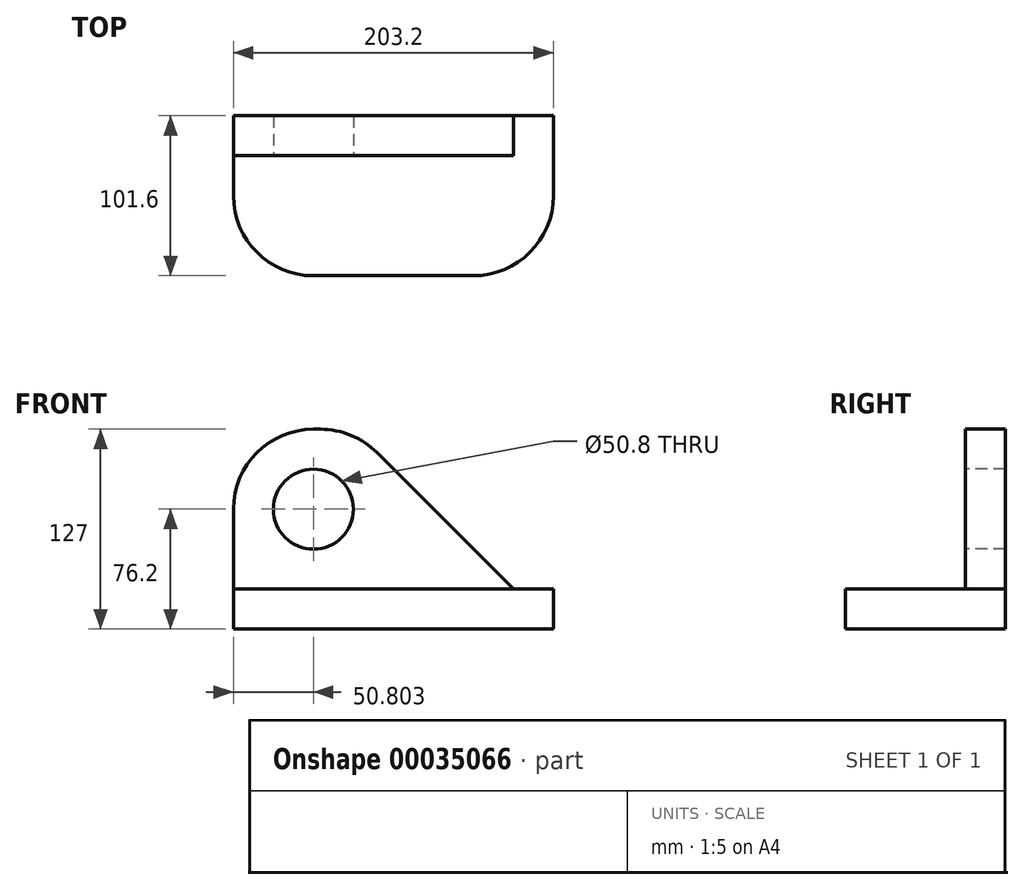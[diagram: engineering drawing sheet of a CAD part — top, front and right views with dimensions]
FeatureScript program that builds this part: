
annotation { "Feature Type Name" : "Feature", "Feature Type Description" : "" }
export const myFeature = defineFeature(function(context is Context, id is Id, definition is map)
    precondition{}
    {
        {
            var Q0;
            Q0=qCreatedBy(makeId("Top.planeOp"),FACE);
            var sketch = newSketch(context, id + "F0", { "sketchPlane" : qUnion([Q0])});
            skLineSegment(sketch, "E0.bottom", {"start": v(-49.18, 40.48) * mm, "end": v(154.02, 40.48) * mm});
            skLineSegment(sketch, "E0.top", {"start": v(-49.18, -61.12) * mm, "end": v(154.02, -61.12) * mm});
            skLineSegment(sketch, "E0.left", {"start": v(-49.18, 40.48) * mm, "end": v(-49.18, -61.12) * mm});
            skLineSegment(sketch, "E0.right", {"start": v(154.02, 40.48) * mm, "end": v(154.02, -61.12) * mm});
            skSolve(sketch);
        }
        {
            var Q0;
            Q0 = qSketchRegion(id + "F0", true);
            var Q1;
            Q1=makeQuery(id+"F0.imprint","IMPRINT",FACE,{"disambiguationData":[TD([[makeQuery(id+"F0.imprint","IMPRINT",EDGE,{"derivedFrom":sQuery(id+"F0.wireOp",EDGE,"E0.bottom")}),-1.0]])]});
            extrude(context, id + "F1", {"entities" : qUnion([Q0, Q1]), "depth" : 25.4 * mm});
        }
        {
            var Q0;
            Q0=makeQuery(id+"F1.opExtrude","SWEPT_EDGE",EDGE,{"disambiguationData":[OSD([sQuery(id+"F0.wireOp",EDGE,"E0.top"),sQuery(id+"F0.wireOp",EDGE,"E0.left")])]});
            var Q1;
            Q1=makeQuery(id+"F1.opExtrude","SWEPT_EDGE",EDGE,{"disambiguationData":[OSD([sQuery(id+"F0.wireOp",EDGE,"E0.top"),sQuery(id+"F0.wireOp",EDGE,"E0.right")])]});
            fillet(context, id + "F2", {"entities" : qUnion([Q0, Q1]), "radius" : 50.8 * mm, "tangentPropagation" : true, "allowEdgeOverflow" : false});
        }
        {
            var Q0;
            Q0=makeQuery(id+"F1.opExtrude","CAP_FACE",FACE,{"disambiguationData":[OSD([sQuery(id+"F0.wireOp",EDGE,"E0.bottom"),sQuery(id+"F0.wireOp",EDGE,"E0.top"),sQuery(id+"F0.wireOp",EDGE,"E0.left"),sQuery(id+"F0.wireOp",EDGE,"E0.right")])],"isStart":false});
            var sketch = newSketch(context, id + "F3", { "sketchPlane" : qUnion([Q0])});
            skLineSegment(sketch, "E1.bottom", {"start": v(-49.18, 40.48) * mm, "end": v(128.62, 40.48) * mm});
            skLineSegment(sketch, "E1.top", {"start": v(-49.18, 15.08) * mm, "end": v(128.62, 15.08) * mm});
            skLineSegment(sketch, "E1.left", {"start": v(-49.18, 40.48) * mm, "end": v(-49.18, 15.08) * mm});
            skLineSegment(sketch, "E1.right", {"start": v(128.62, 40.48) * mm, "end": v(128.62, 15.08) * mm});
            skSolve(sketch);
        }
        {
            var Q0;
            Q0=makeQuery(id+"F3.imprint","IMPRINT",FACE,{"disambiguationData":[TD([[makeQuery(id+"F3.imprint","IMPRINT",EDGE,{"derivedFrom":sQuery(id+"F3.wireOp",EDGE,"E1.bottom")}),-1.0]])]});
            extrude(context, id + "F4", {"entities" : qUnion([Q0]), "operationType" : NewBodyOperationType.ADD, "depth" : 25.4 * mm});
        }
        {
            var Q0;
            Q0 = qSketchRegion(id + "F3", true);
            extrude(context, id + "F5", {"entities" : qUnion([Q0]), "operationType" : NewBodyOperationType.ADD, "depth" : 101.6 * mm});
        }
        {
            var Q0;
            Q0=makeQuery(id+"F5.opExtrude","CAP_EDGE",EDGE,{"disambiguationData":[OSD([sQuery(id+"F3.wireOp",EDGE,"E1.right")])],"isStart":false});
            chamfer(context, id + "F6", {"entities" : qUnion([Q0]), "chamferType" : ChamferType.TWO_OFFSETS, "width1" : 101.6 * mm, "oppositeDirection" : false, "width2" : 101.6 * mm, "tangentPropagation" : true});
        }
        {
            var Q0;
            Q0=makeQuery(id+"F5.opExtrude","CAP_EDGE",EDGE,{"disambiguationData":[OSD([sQuery(id+"F3.wireOp",EDGE,"E1.left")])],"isStart":false});
            var Q1;
            {var subQ0=sQuery(id+"F3.wireOp",EDGE,"E1.right");Q1=makeQuery(id+"F6.opChamfer","BLEND_EDGE",EDGE,{"blendedFrom":[makeQuery(id+"F5.opExtrude","CAP_EDGE",EDGE,{"disambiguationData":[OSD([subQ0])],"isStart":false}),makeQuery(id+"F5.opExtrude","CAP_FACE",FACE,{"disambiguationData":[OSD([sQuery(id+"F3.wireOp",EDGE,"E1.bottom"),sQuery(id+"F3.wireOp",EDGE,"E1.top"),sQuery(id+"F3.wireOp",EDGE,"E1.left"),subQ0])],"isStart":false})],"blendedInto":[makeQuery(id+"F5.opExtrude","CAP_FACE",FACE,{"disambiguationData":[OSD([sQuery(id+"F3.wireOp",EDGE,"E1.bottom"),sQuery(id+"F3.wireOp",EDGE,"E1.top"),sQuery(id+"F3.wireOp",EDGE,"E1.left"),subQ0])],"isStart":false})]});}
            fillet(context, id + "F7", {"entities" : qUnion([Q0, Q1]), "radius" : 50.8 * mm, "tangentPropagation" : true, "allowEdgeOverflow" : false});
        }
        {
            var Q0;
            {var subQ0=sQuery(id+"F3.wireOp",EDGE,"E1.top");Q0=makeQuery(id+"F5.boolean.opBoolean","MERGE",FACE,{"derivedFrom":[makeQuery(id+"F4.opExtrude","SWEPT_FACE",FACE,{"disambiguationData":[OSD([subQ0])]}),makeQuery(id+"F5.opExtrude","SWEPT_FACE",FACE,{"disambiguationData":[OSD([subQ0])]})]});}
            var sketch = newSketch(context, id + "F8", { "sketchPlane" : qUnion([Q0])});
            skLineSegment(sketch, "E2", {"start": v(-49.18, 76.2) * mm, "end": v(1.62, 76.2) * mm});
            skSolve(sketch);
        }
        {
            var Q0;
            Q0=sQuery(id+"F8.wireOp",VERTEX,"E2.end");
            var Q1;
            Q1=makeQuery(id+"F1.opExtrude","SWEPT_BODY",BODY,{"disambiguationData":[OSD([sQuery(id+"F0.wireOp",EDGE,"E0.bottom"),sQuery(id+"F0.wireOp",EDGE,"E0.top"),sQuery(id+"F0.wireOp",EDGE,"E0.left"),sQuery(id+"F0.wireOp",EDGE,"E0.right")])]});
            hole(context, id + "F9", {"style" : HoleStyle.SIMPLE, "holeDiameter" : 50.8 * mm, "endStyle" : HoleEndStyle.THROUGH, "locations" : qUnion([Q0]), "scope" : qUnion([Q1])});
        }
    });
